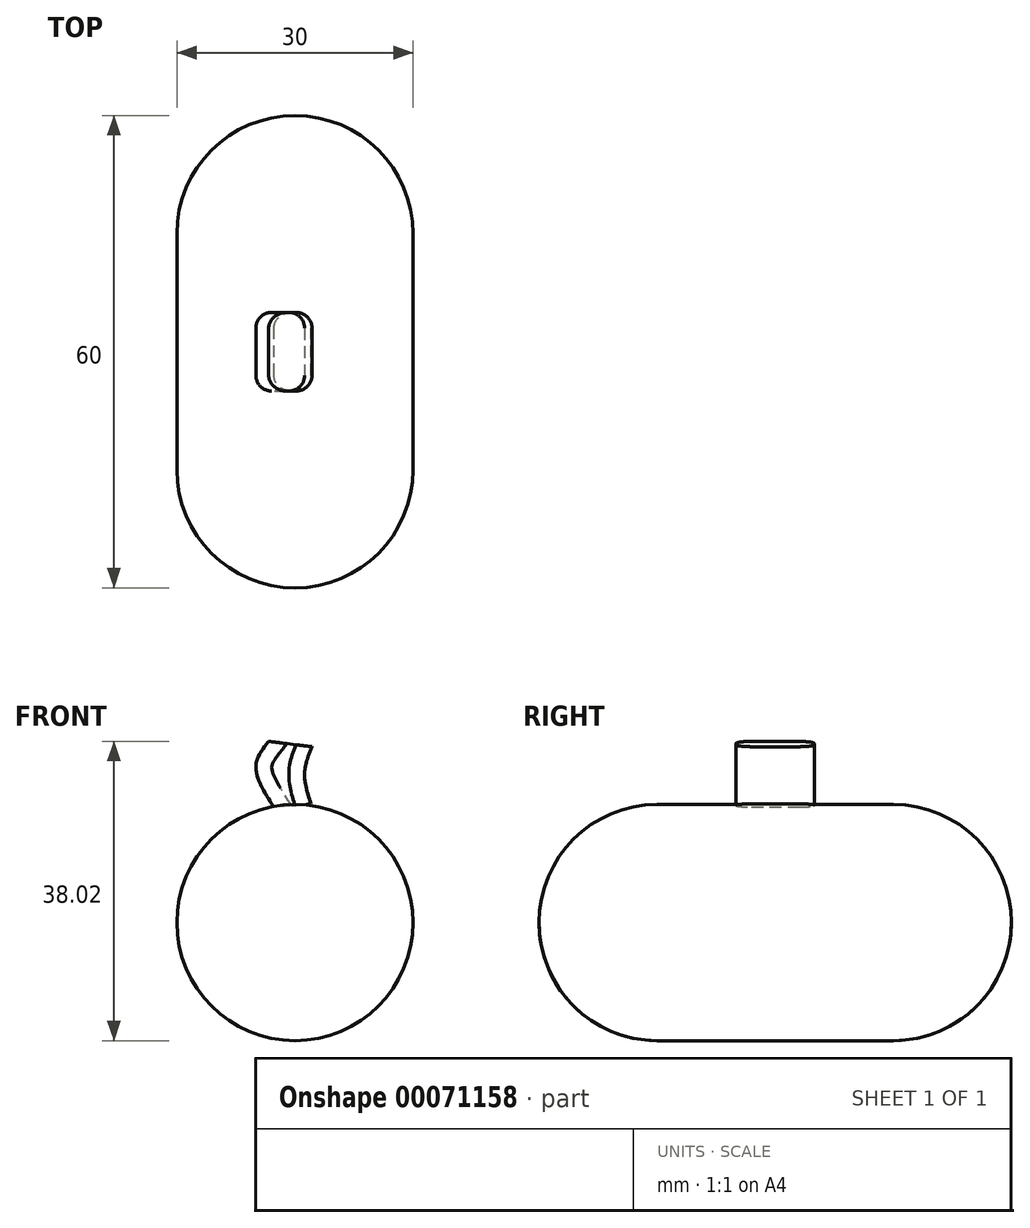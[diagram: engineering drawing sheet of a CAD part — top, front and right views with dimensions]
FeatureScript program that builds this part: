
annotation { "Feature Type Name" : "Feature", "Feature Type Description" : "" }
export const myFeature = defineFeature(function(context is Context, id is Id, definition is map)
    precondition{}
    {
        {
            var Q0;
            Q0=qCreatedBy(makeId("Front.planeOp"),FACE);
            var sketch = newSketch(context, id + "F0", { "sketchPlane" : qUnion([Q0])});
            skCircle(sketch, "E0", {"center": v(0, 0) * mm, "radius": 15 * mm});
            skSolve(sketch);
        }
        {
            var Q0;
            Q0=makeQuery(id+"F0.imprint","IMPRINT",FACE,{"disambiguationData":[TD([[makeQuery(id+"F0.imprint","IMPRINT",EDGE,{"derivedFrom":sQuery(id+"F0.wireOp",EDGE,"E0")}),1.0]])]});
            extrude(context, id + "F1", {"entities" : qUnion([Q0]), "endBound" : BoundingType.SYMMETRIC, "depth" : 60 * mm});
        }
        {
            var Q0;
            Q0=makeQuery(id+"F1.opExtrude","CAP_FACE",FACE,{"disambiguationData":[OSD([sQuery(id+"F0.wireOp",EDGE,"E0")])],"isStart":false});
            fillet(context, id + "F2", {"entities" : qUnion([Q0]), "radius" : 15 * mm, "tangentPropagation" : true, "allowEdgeOverflow" : false});
        }
        {
            var Q0;
            Q0=makeQuery(id+"F1.opExtrude","CAP_FACE",FACE,{"disambiguationData":[OSD([sQuery(id+"F0.wireOp",EDGE,"E0")])],"isStart":true});
            fillet(context, id + "F3", {"entities" : qUnion([Q0]), "radius" : 15 * mm, "tangentPropagation" : true, "allowEdgeOverflow" : false});
        }
        {
            var Q0;
            Q0=qCreatedBy(makeId("Front.planeOp"),FACE);
            var sketch = newSketch(context, id + "F4", { "sketchPlane" : qUnion([Q0])});
            skFitSpline(sketch, "E1", {"points": [v(-2.67, 14.67) * mm, v(-4.96, 19.79) * mm, v(-3.35, 23.02) * mm], "startDerivative": vector(-6.27, 9.76) * mm, "endDerivative": vector(5.35, 6.81) * mm});
            skFitSpline(sketch, "E2", {"points": [v(2.04, 15.08) * mm, v(1.23, 18.98) * mm, v(2.17, 22.34) * mm], "startDerivative": vector(-2.47, 7.71) * mm, "endDerivative": vector(2.8, 6.81) * mm});
            skLineSegment(sketch, "E3", {"start": v(-3.35, 23.02) * mm, "end": v(2.17, 22.34) * mm});
            skLineSegment(sketch, "E4", {"start": v(-2.67, 14.67) * mm, "end": v(2.04, 15.08) * mm});
            skSolve(sketch);
        }
        {
            var Q0;
            Q0 = qSketchRegion(id + "F4", true);
            extrude(context, id + "F5", {"entities" : qUnion([Q0]), "endBound" : BoundingType.SYMMETRIC, "depth" : 10 * mm});
        }
        {
            var Q0;
            Q0=makeQuery(id+"F5.opExtrude","CAP_EDGE",EDGE,{"disambiguationData":[OSD([sQuery(id+"F4.wireOp",EDGE,"E2")])],"isStart":true});
            var Q1;
            Q1=makeQuery(id+"F5.opExtrude","CAP_EDGE",EDGE,{"disambiguationData":[OSD([sQuery(id+"F4.wireOp",EDGE,"E2")])],"isStart":false});
            var Q2;
            Q2=makeQuery(id+"F5.opExtrude","CAP_EDGE",EDGE,{"disambiguationData":[OSD([sQuery(id+"F4.wireOp",EDGE,"E1")])],"isStart":true});
            var Q3;
            Q3=makeQuery(id+"F5.opExtrude","CAP_EDGE",EDGE,{"disambiguationData":[OSD([sQuery(id+"F4.wireOp",EDGE,"E1")])],"isStart":false});
            fillet(context, id + "F6", {"entities" : qUnion([Q0, Q1, Q2, Q3]), "radius" : 2 * mm, "tangentPropagation" : true, "allowEdgeOverflow" : false});
        }
    });
